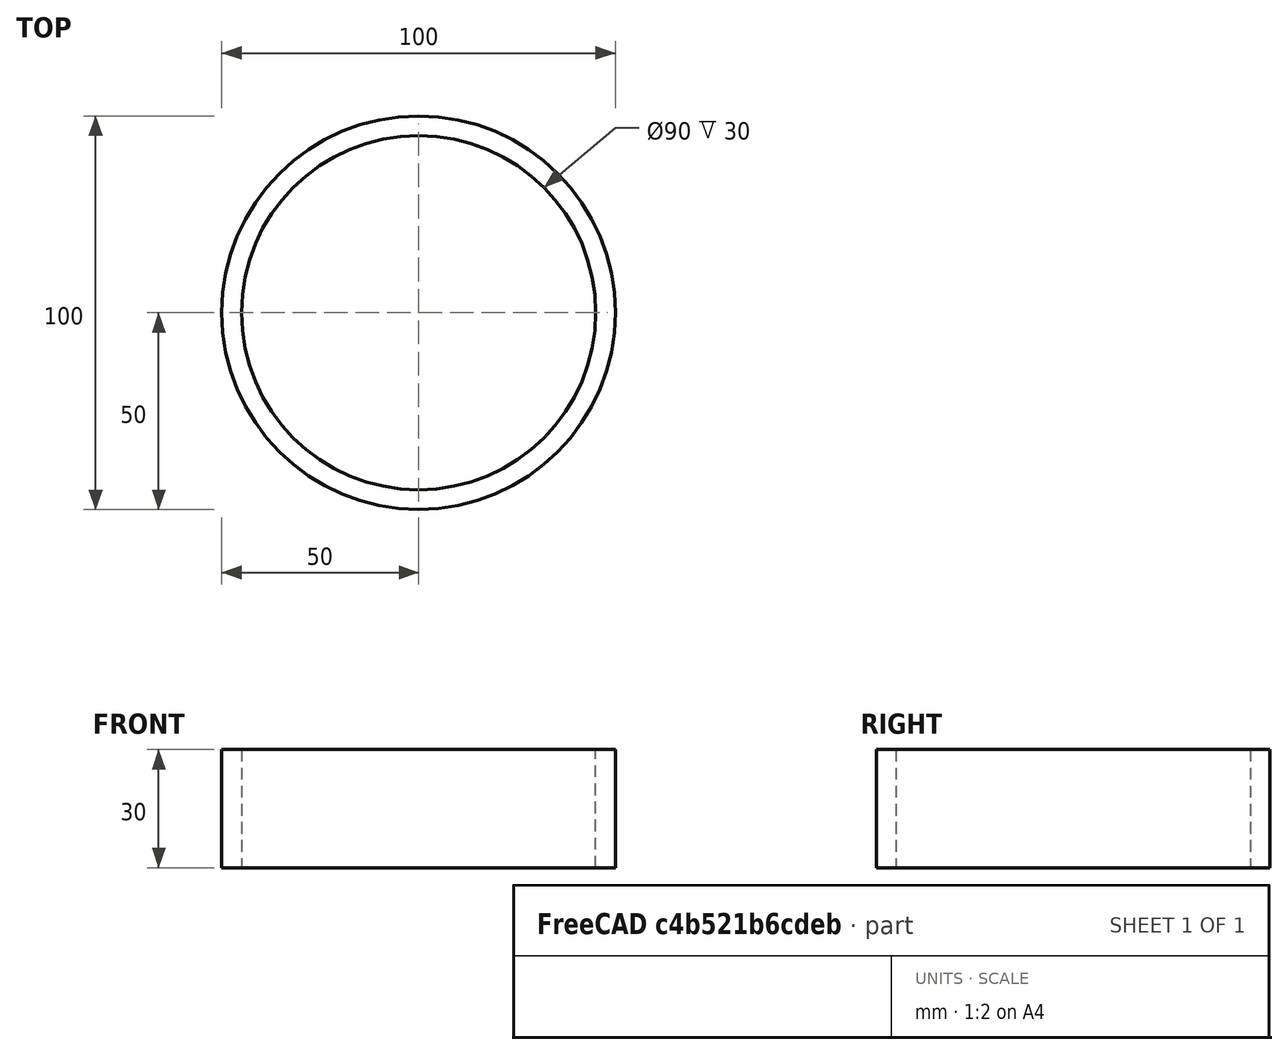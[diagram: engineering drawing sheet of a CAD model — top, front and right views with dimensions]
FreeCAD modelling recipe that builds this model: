
FCSTD DOCUMENT  (FreeCAD 1.0R39319 (Git))
Label: outer_ring
License: Public Domain
LicenseURL: https://en.wikipedia.org/wiki/Public_domain
objects: Sketcher::SketchObject×1, PartDesign::Pad×1, PartDesign::Body×1
note: 6 computed .brp shape members not serialized (recipe doc carries the construction recipe); baked Part::Feature solids carry a one-line shape summary decoded from their .brp

FEATURE [Sketcher::SketchObject] Sketch
  ArcFitTolerance = 1e-06
  AttachmentSupport = -> [Origin]
  FullyConstrained = true
  MakeInternals = false
  MapMode = 5
  sketch-geometry (3):
    g0: GeomPoint X=0 Y=0 Z=0
    g1: Circle CenterX=0 CenterY=0 CenterZ=0 NormalX=0 NormalY=0 NormalZ=1 AngleXU=0 Radius=45
    g2: Circle CenterX=0 CenterY=0 CenterZ=0 NormalX=0 NormalY=0 NormalZ=1 AngleXU=0 Radius=50
  constraints (5):
    c: Coincident(g0,g-1)
    c: Diameter(g1) = 90
    c: Coincident(g1,g0)
    c: Diameter(g2) = 100
    c: Coincident(g2,g0)
FEATURE [PartDesign::Pad] Pad
  Direction = (0,0,1)
  Length = 30
  Length2 = 10
  Profile = -> Sketch
  ReferenceAxis = -> Sketch [N_Axis]
  Refine = true
  Suppressed = false
  Type = 0
FEATURE [PartDesign::Body] Body
  AllowCompound = true
  Group = -> [Sketch,Pad]
  Origin = -> Origin
  Tip = -> Pad
